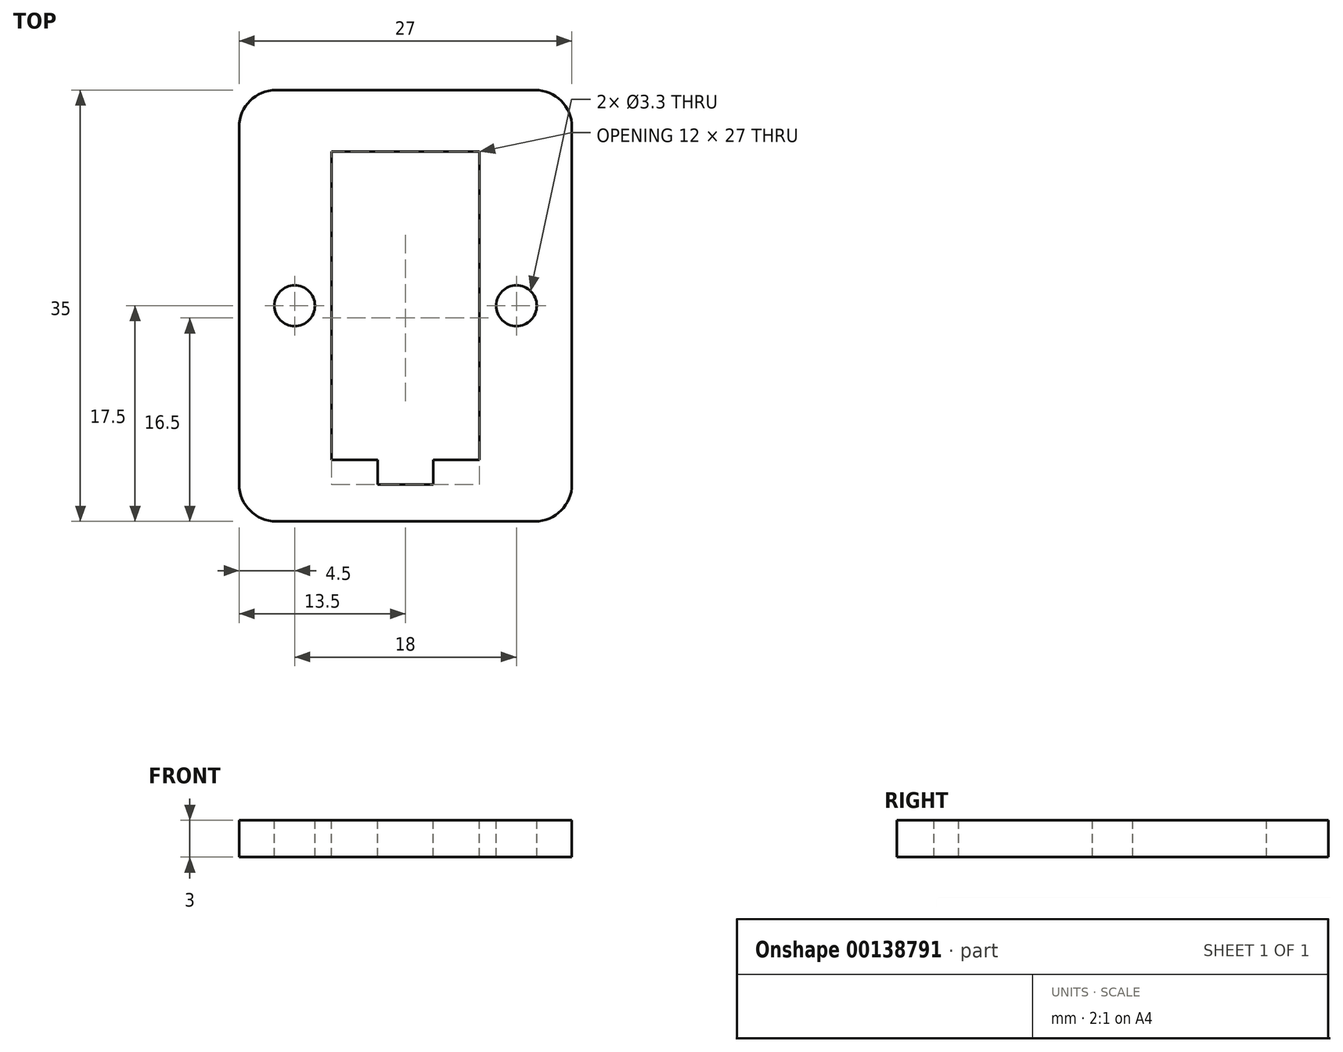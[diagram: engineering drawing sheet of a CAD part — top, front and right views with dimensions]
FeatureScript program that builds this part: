
annotation { "Feature Type Name" : "Feature", "Feature Type Description" : "" }
export const myFeature = defineFeature(function(context is Context, id is Id, definition is map)
    precondition{}
    {
        {
            var Q0;
            Q0=qCreatedBy(makeId("Top.planeOp"),FACE);
            var sketch = newSketch(context, id + "F0", { "sketchPlane" : qUnion([Q0])});
            skLineSegment(sketch, "E0.bottom", {"start": v(-10.5, 17.5) * mm, "end": v(10.5, 17.5) * mm});
            skLineSegment(sketch, "E0.top", {"start": v(-10.5, -17.5) * mm, "end": v(10.5, -17.5) * mm});
            skLineSegment(sketch, "E0.left", {"start": v(-13.5, 14.5) * mm, "end": v(-13.5, -14.5) * mm});
            skLineSegment(sketch, "E0.right", {"start": v(13.5, 14.5) * mm, "end": v(13.5, -14.5) * mm});
            skPoint(sketch, "E0.middle", {"position": v(0, 0) * mm});
            skPoint(sketch, "E1.visualSharp", {"position": v(-13.5, 17.5) * mm});
            skArc(sketch, "E1.filletArc", {"start": v(-10.5, 17.5) * mm, "mid": v(-12.62, 16.62) * mm, "end": v(-13.5, 14.5) * mm});
            skPoint(sketch, "E2.visualSharp", {"position": v(13.5, 17.5) * mm});
            skArc(sketch, "E2.filletArc", {"start": v(13.5, 14.5) * mm, "mid": v(12.62, 16.62) * mm, "end": v(10.5, 17.5) * mm});
            skPoint(sketch, "E3.visualSharp", {"position": v(13.5, -17.5) * mm});
            skArc(sketch, "E3.filletArc", {"start": v(10.5, -17.5) * mm, "mid": v(12.62, -16.62) * mm, "end": v(13.5, -14.5) * mm});
            skPoint(sketch, "E4.visualSharp", {"position": v(-13.5, -17.5) * mm});
            skArc(sketch, "E4.filletArc", {"start": v(-13.5, -14.5) * mm, "mid": v(-12.62, -16.62) * mm, "end": v(-10.5, -17.5) * mm});
            skSolve(sketch);
        }
        {
            var Q0;
            Q0=qSketchRegion(id+"F0",true);
            extrude(context, id + "F1", {"entities" : qUnion([Q0]), "depth" : 3 * mm});
        }
        {
            var Q0;
            Q0=makeQuery(id+"F1.opExtrude","CAP_FACE",FACE,{"disambiguationData":[OSD([sQuery(id+"F0.wireOp",EDGE,"E0.bottom"),sQuery(id+"F0.wireOp",EDGE,"E0.top"),sQuery(id+"F0.wireOp",EDGE,"E0.left"),sQuery(id+"F0.wireOp",EDGE,"E0.right"),sQuery(id+"F0.wireOp",EDGE,"E1.filletArc"),sQuery(id+"F0.wireOp",EDGE,"E2.filletArc"),sQuery(id+"F0.wireOp",EDGE,"E3.filletArc"),sQuery(id+"F0.wireOp",EDGE,"E4.filletArc")])],"isStart":false});
            var sketch = newSketch(context, id + "F2", { "sketchPlane" : qUnion([Q0])});
            skCircle(sketch, "E5", {"center": v(-9, 0) * mm, "radius": 1.65 * mm});
            skCircle(sketch, "E6", {"center": v(9, 0) * mm, "radius": 1.65 * mm});
            skSolve(sketch);
        }
        {
            var Q0;
            Q0=sQuery(id+"F2.wireOp",VERTEX,"E5.center");
            var Q1;
            Q1=sQuery(id+"F2.wireOp",VERTEX,"E6.center");
            var Q2;
            Q2=makeQuery(id+"F1.opExtrude","SWEPT_BODY",BODY,{"disambiguationData":[OSD([sQuery(id+"F0.wireOp",EDGE,"E0.bottom"),sQuery(id+"F0.wireOp",EDGE,"E0.top"),sQuery(id+"F0.wireOp",EDGE,"E0.left"),sQuery(id+"F0.wireOp",EDGE,"E0.right"),sQuery(id+"F0.wireOp",EDGE,"E1.filletArc"),sQuery(id+"F0.wireOp",EDGE,"E2.filletArc"),sQuery(id+"F0.wireOp",EDGE,"E3.filletArc"),sQuery(id+"F0.wireOp",EDGE,"E4.filletArc")])]});
            hole(context, id + "F3", {"style" : HoleStyle.SIMPLE, "endStyle" : HoleEndStyle.THROUGH, "holeDiameter" : 3.3 * mm, "locations" : qUnion([Q0, Q1]), "scope" : qUnion([Q2]), "isTappedThrough" : true});
        }
        {
            var Q0;
            Q0=makeQuery(id+"F1.opExtrude","CAP_FACE",FACE,{"disambiguationData":[OSD([sQuery(id+"F0.wireOp",EDGE,"E0.bottom"),sQuery(id+"F0.wireOp",EDGE,"E0.top"),sQuery(id+"F0.wireOp",EDGE,"E0.left"),sQuery(id+"F0.wireOp",EDGE,"E0.right"),sQuery(id+"F0.wireOp",EDGE,"E1.filletArc"),sQuery(id+"F0.wireOp",EDGE,"E2.filletArc"),sQuery(id+"F0.wireOp",EDGE,"E3.filletArc"),sQuery(id+"F0.wireOp",EDGE,"E4.filletArc")])],"isStart":false});
            var sketch = newSketch(context, id + "F4", { "sketchPlane" : qUnion([Q0])});
            skLineSegment(sketch, "E7.bottom", {"start": v(-6, 12.5) * mm, "end": v(6, 12.5) * mm});
            skLineSegment(sketch, "E7.top", {"start": v(-6, -12.5) * mm, "end": v(-2.25, -12.5) * mm});
            skLineSegment(sketch, "E7.left", {"start": v(-6, 12.5) * mm, "end": v(-6, -12.5) * mm});
            skLineSegment(sketch, "E7.right", {"start": v(6, 12.5) * mm, "end": v(6, -12.5) * mm});
            skPoint(sketch, "E7.middle", {"position": v(0, 0) * mm});
            skLineSegment(sketch, "E8.bottom", {"start": v(-2.25, -14.5) * mm, "end": v(2.25, -14.5) * mm});
            skLineSegment(sketch, "E8.left", {"start": v(-2.25, -14.5) * mm, "end": v(-2.25, -12.5) * mm});
            skLineSegment(sketch, "E8.right", {"start": v(2.25, -14.5) * mm, "end": v(2.25, -12.5) * mm});
            skLineSegment(sketch, "E9.trimOffspring", {"start": v(2.25, -12.5) * mm, "end": v(6, -12.5) * mm});
            skSolve(sketch);
        }
        {
            var Q0;
            Q0=qSketchRegion(id+"F4",true);
            extrude(context, id + "F5", {"entities" : qUnion([Q0]), "operationType" : NewBodyOperationType.REMOVE, "endBound" : BoundingType.THROUGH_ALL, "oppositeDirection" : true, "depth" : 25 * mm});
        }
    });
